# Revit family: RTU-Hydronic-Carrier-50V-Compact_Chassis-27_35_ton
name_source: partatom
category: Mechanical Equipment
units: mm (PartAtom-declared; Revit-internal decimal feet)

## family parameters
Always vertical = Yes
Cut with Voids When Loaded = No
OmniClass Number = 23.75.35.14.14
OmniClass Title = Customized Rooftop Air Handling Units
Part Type = Normal
Room Calculation Point = No
Round Connector Dimension = Use Diameter
Shared = No
Work Plane-Based = Yes

## types (1)
- By Type
    Assembly Code = D3060300
    Condensate Drain Connection Diameter = 3"
    Condensate Drain Connection Diameter Description = 2-1/2" x 2" NPS Condensate Drain Connection
    Dead Weight = 0
    Default Elevation = 0 mm  [stored 0 ft]
    Description = TBD
    EER = 0
    Efficiency Ratings = by Type
    Electrical_Wattage = 0 W
    Gas Fuel = No
    Gas Line Pressure Range = 5 - 13.5 in wg
    Horizontal Air Connections = No
    Hot Water Coil Connection Diameter = 3"
    Hot Water Coil Connection Diameter Description = 2x 2/12" NPT Hot Water Coil Conn
    Hot Water Fuel = Yes
    IEER = 0
    Keynote = 23 75 00
    Length = 5283 mm
    Manufacturer = Carrier
    Model = TBD
    Nominal Capacity = by Type
    Operating Temperature Range = 40 - 115 F Standard. 25 F with options.
    Product Name = 50V
    Refrigerant Used = R410A
    SEER = 0
    Sensible Cooling Capacity = 0.0 Btu/h
    Standards Conformance = By Type
    URL = https://www.carrier.com
    Width = 2370 mm  [stored 7.77559 ft]

note: [stored X ft] marks values corroborated as IEEE doubles in the binary element streams (Revit-internal decimal feet)

## geometry (parser evidence)
native form markers: Sweep x13
no freeform markers — native parametric forms only
